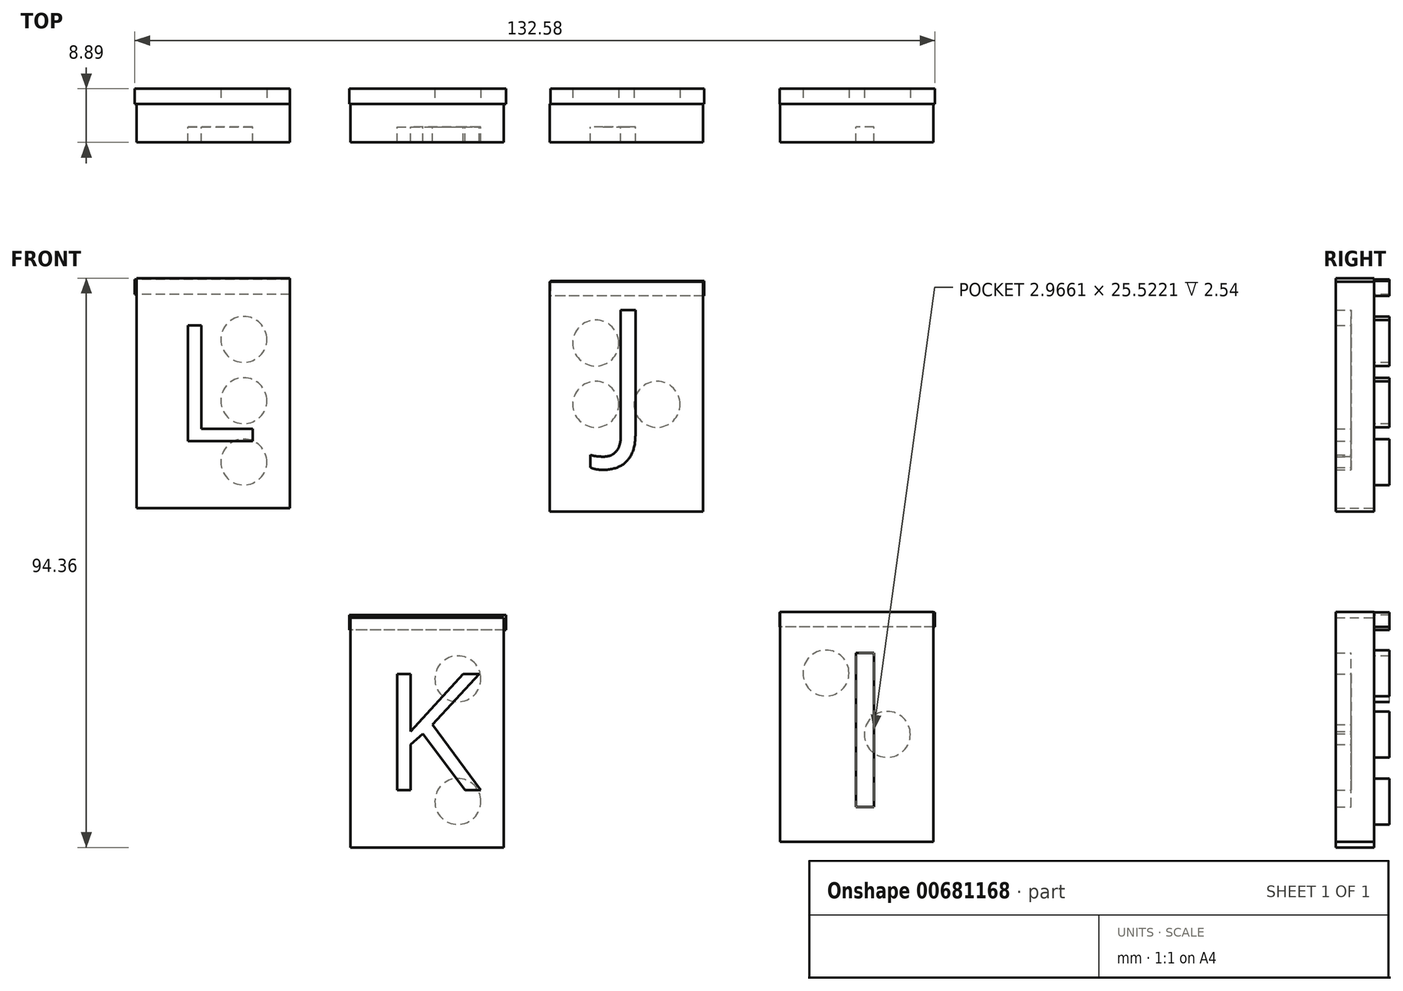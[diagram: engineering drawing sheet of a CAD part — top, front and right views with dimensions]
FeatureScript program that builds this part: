
annotation { "Feature Type Name" : "Feature", "Feature Type Description" : "" }
export const myFeature = defineFeature(function(context is Context, id is Id, definition is map)
    precondition{}
    {
        {
            var Q0;
            Q0=qCreatedBy(makeId("Front.planeOp"),FACE);
            var sketch = newSketch(context, id + "F0", { "sketchPlane" : qUnion([Q0])});
            skLineSegment(sketch, "E0.bottom", {"start": v(-58.76, 38.35) * mm, "end": v(-33.36, 38.35) * mm});
            skLineSegment(sketch, "E0.top", {"start": v(-58.76, 0.25) * mm, "end": v(-33.36, 0.25) * mm});
            skLineSegment(sketch, "E0.left", {"start": v(-58.76, 38.35) * mm, "end": v(-58.76, 0.25) * mm});
            skLineSegment(sketch, "E0.right", {"start": v(-33.36, 38.35) * mm, "end": v(-33.36, 0.25) * mm});
            skLineSegment(sketch, "E1.bottom", {"start": v(-23.3, -17.91) * mm, "end": v(2.1, -17.91) * mm});
            skLineSegment(sketch, "E1.top", {"start": v(-23.3, -56.01) * mm, "end": v(2.1, -56.01) * mm});
            skLineSegment(sketch, "E1.left", {"start": v(-23.3, -17.91) * mm, "end": v(-23.3, -56.01) * mm});
            skLineSegment(sketch, "E1.right", {"start": v(2.1, -17.91) * mm, "end": v(2.1, -56.01) * mm});
            skLineSegment(sketch, "E2.bottom", {"start": v(47.85, -16.96) * mm, "end": v(73.25, -16.96) * mm});
            skLineSegment(sketch, "E2.top", {"start": v(47.85, -55.06) * mm, "end": v(73.25, -55.06) * mm});
            skLineSegment(sketch, "E2.left", {"start": v(47.85, -16.96) * mm, "end": v(47.85, -55.06) * mm});
            skLineSegment(sketch, "E2.right", {"start": v(73.25, -16.96) * mm, "end": v(73.25, -55.06) * mm});
            skLineSegment(sketch, "E3.bottom", {"start": v(9.7, 37.75) * mm, "end": v(35.1, 37.75) * mm});
            skLineSegment(sketch, "E3.top", {"start": v(9.7, -0.35) * mm, "end": v(35.1, -0.35) * mm});
            skLineSegment(sketch, "E3.left", {"start": v(9.7, 37.75) * mm, "end": v(9.7, -0.35) * mm});
            skLineSegment(sketch, "E3.right", {"start": v(35.1, 37.75) * mm, "end": v(35.1, -0.35) * mm});
            skSolve(sketch);
        }
        {
            var Q0;
            Q0=qSketchRegion(id+"F0",true);
            extrude(context, id + "F1", {"entities" : qUnion([Q0]), "depth" : 6.35 * mm});
        }
        {
            var Q0;
            Q0=qCreatedBy(makeId("Front.planeOp"),FACE);
            var sketch = newSketch(context, id + "F2", { "sketchPlane" : qUnion([Q0])});
            skCircle(sketch, "E4", {"center": v(27.49, 17.43) * mm, "radius": 3.81 * mm});
            skCircle(sketch, "E5", {"center": v(65.63, -37.28) * mm, "radius": 3.81 * mm});
            skCircle(sketch, "E6", {"center": v(-5.52, -28.07) * mm, "radius": 3.81 * mm});
            skCircle(sketch, "E7", {"center": v(17.33, 27.59) * mm, "radius": 3.81 * mm});
            skCircle(sketch, "E8", {"center": v(17.33, 17.43) * mm, "radius": 3.81 * mm});
            skCircle(sketch, "E9", {"center": v(-5.52, -48.4) * mm, "radius": 3.8 * mm});
            skCircle(sketch, "E10", {"center": v(-40.98, 28.19) * mm, "radius": 3.81 * mm});
            skCircle(sketch, "E11", {"center": v(-40.98, 18.03) * mm, "radius": 3.81 * mm});
            skCircle(sketch, "E12", {"center": v(-40.98, 7.87) * mm, "radius": 3.81 * mm});
            skCircle(sketch, "E13", {"center": v(55.47, -27.12) * mm, "radius": 3.81 * mm});
            skSolve(sketch);
        }
        {
            var Q0;
            Q0=qSketchRegion(id+"F2",true);
            extrude(context, id + "F3", {"entities" : qUnion([Q0]), "operationType" : NewBodyOperationType.ADD, "oppositeDirection" : true, "depth" : 2.54 * mm});
        }
        {
            var Q0;
            Q0=qCreatedBy(makeId("Front.planeOp"),FACE);
            cPlane(context, id + "F4", {"entities" : qUnion([Q0]), "cplaneType" : CPlaneType.OFFSET, "offset" : 3.8 * mm, "width" : 152.4 * mm, "height" : 152.4 * mm});
        }
        {
            var Q0;
            Q0=qCreatedBy(id+"F4.planeOp",FACE);
            var sketch = newSketch(context, id + "F5", { "sketchPlane" : qUnion([Q0])});
            skText(sketch, "E14", { "text": "I", "fontName": "OpenSans-Regular.ttf"});
            skText(sketch, "E15", { "text": "J", "fontName": "OpenSans-Regular.ttf"});
            skText(sketch, "E16", { "text": "K", "fontName": "OpenSans-Regular.ttf"});
            skText(sketch, "E17", { "text": "L", "fontName": "OpenSans-Regular.ttf"});
            const initialGuessF5  = {"E14": [0.05695, -0.0493, 1, 0, 0.02574], "E15": [0.01873, 0.0121, 1, 0, 0.02115], "E16": [-0.01822, -0.0465, 1, 0, 0.01937], "E17": [-0.05287, 0.01134, 1, 0, 0.01937]};
            skSetInitialGuess(sketch, initialGuessF5);
            skSolve(sketch);
        }
        {
            var Q0;
            Q0=qSketchRegion(id+"F5",true);
            extrude(context, id + "F6", {"entities" : qUnion([Q0]), "operationType" : NewBodyOperationType.REMOVE, "depth" : 25.4 * mm});
        }
        {
            var Q0;
            Q0=qCreatedBy(makeId("Front.planeOp"),FACE);
            var sketch = newSketch(context, id + "F7", { "sketchPlane" : qUnion([Q0])});
            skLineSegment(sketch, "E18.bottom", {"start": v(73.52, -17.03) * mm, "end": v(47.79, -17.03) * mm});
            skLineSegment(sketch, "E18.top", {"start": v(73.52, -19.48) * mm, "end": v(47.79, -19.48) * mm});
            skLineSegment(sketch, "E18.left", {"start": v(73.52, -17.03) * mm, "end": v(73.52, -19.48) * mm});
            skLineSegment(sketch, "E18.right", {"start": v(47.79, -17.03) * mm, "end": v(47.79, -19.48) * mm});
            skLineSegment(sketch, "E19.bottom", {"start": v(35.29, 37.86) * mm, "end": v(9.8, 37.86) * mm});
            skLineSegment(sketch, "E19.top", {"start": v(35.29, 35.41) * mm, "end": v(9.8, 35.41) * mm});
            skLineSegment(sketch, "E19.left", {"start": v(35.29, 37.86) * mm, "end": v(35.29, 35.41) * mm});
            skLineSegment(sketch, "E19.right", {"start": v(9.8, 37.86) * mm, "end": v(9.8, 35.41) * mm});
            skLineSegment(sketch, "E20.bottom", {"start": v(-33.33, 38.1) * mm, "end": v(-59.06, 38.1) * mm});
            skLineSegment(sketch, "E20.top", {"start": v(-33.33, 35.66) * mm, "end": v(-59.06, 35.66) * mm});
            skLineSegment(sketch, "E20.left", {"start": v(-33.33, 38.1) * mm, "end": v(-33.33, 35.66) * mm});
            skLineSegment(sketch, "E20.right", {"start": v(-59.06, 38.1) * mm, "end": v(-59.06, 35.66) * mm});
            skLineSegment(sketch, "E21.bottom", {"start": v(2.45, -17.52) * mm, "end": v(-23.53, -17.52) * mm});
            skLineSegment(sketch, "E21.top", {"start": v(2.45, -19.97) * mm, "end": v(-23.53, -19.97) * mm});
            skLineSegment(sketch, "E21.left", {"start": v(2.45, -17.52) * mm, "end": v(2.45, -19.97) * mm});
            skLineSegment(sketch, "E21.right", {"start": v(-23.53, -17.52) * mm, "end": v(-23.53, -19.97) * mm});
            skSolve(sketch);
        }
        {
            var Q0;
            Q0=qSketchRegion(id+"F7",true);
            extrude(context, id + "F8", {"entities" : qUnion([Q0]), "operationType" : NewBodyOperationType.ADD, "oppositeDirection" : true, "depth" : 2.54 * mm});
        }
    });
